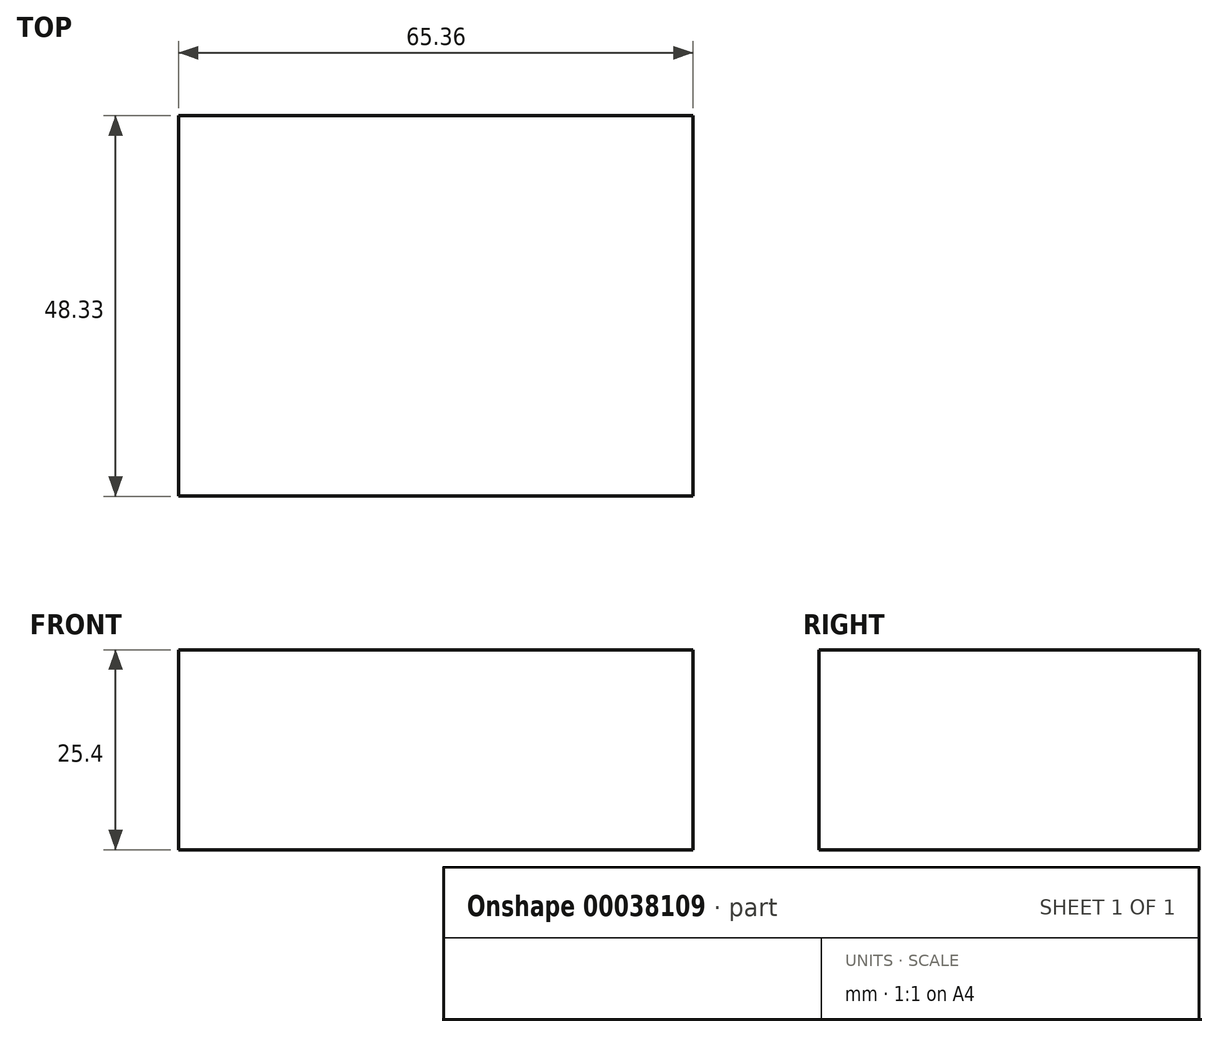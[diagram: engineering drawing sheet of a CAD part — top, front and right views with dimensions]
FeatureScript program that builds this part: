
annotation { "Feature Type Name" : "Feature", "Feature Type Description" : "" }
export const myFeature = defineFeature(function(context is Context, id is Id, definition is map)
    precondition{}
    {
        {
            var Q0;
            Q0=qCreatedBy(makeId("Top.planeOp"),FACE);
            var sketch = newSketch(context, id + "F0", { "sketchPlane" : qUnion([Q0])});
            skLineSegment(sketch, "E0.bottom", {"start": v(-32.88, 23.57) * mm, "end": v(32.48, 23.57) * mm});
            skLineSegment(sketch, "E0.top", {"start": v(-32.88, -24.76) * mm, "end": v(32.48, -24.76) * mm});
            skLineSegment(sketch, "E0.left", {"start": v(-32.88, 23.57) * mm, "end": v(-32.88, -24.76) * mm});
            skLineSegment(sketch, "E0.right", {"start": v(32.48, 23.57) * mm, "end": v(32.48, -24.76) * mm});
            skSolve(sketch);
        }
        {
            var Q0;
            Q0=makeQuery(id+"F0.imprint","IMPRINT",FACE,{"disambiguationData":[TD([[makeQuery(id+"F0.imprint","IMPRINT",EDGE,{"derivedFrom":sQuery(id+"F0.wireOp",EDGE,"E0.bottom")}),-1.0]])]});
            var Q1;
            Q1 = qSketchRegion(id + "F0", true);
            extrude(context, id + "F1", {"entities" : qUnion([Q0, Q1]), "depth" : 25.4 * mm});
        }
        {
            var Q0;
            Q0=makeQuery(id+"F1.opExtrude","CAP_FACE",FACE,{"disambiguationData":[OSD([sQuery(id+"F0.wireOp",EDGE,"E0.bottom"),sQuery(id+"F0.wireOp",EDGE,"E0.top"),sQuery(id+"F0.wireOp",EDGE,"E0.left"),sQuery(id+"F0.wireOp",EDGE,"E0.right")])],"isStart":false});
            var sketch = newSketch(context, id + "F2", { "sketchPlane" : qUnion([Q0])});
            skCircle(sketch, "E1", {"center": v(0, 0) * mm, "radius": 12.66 * mm});
            skSolve(sketch);
        }
        {
            var Q0;
            Q0=sQuery(id+"F2.wireOp",EDGE,"E1");
            extrude(context, id + "F3", {"bodyType" : ToolBodyType.SURFACE, "surfaceEntities" : qUnion([Q0]), "depth" : 25.4 * mm});
        }
    });
